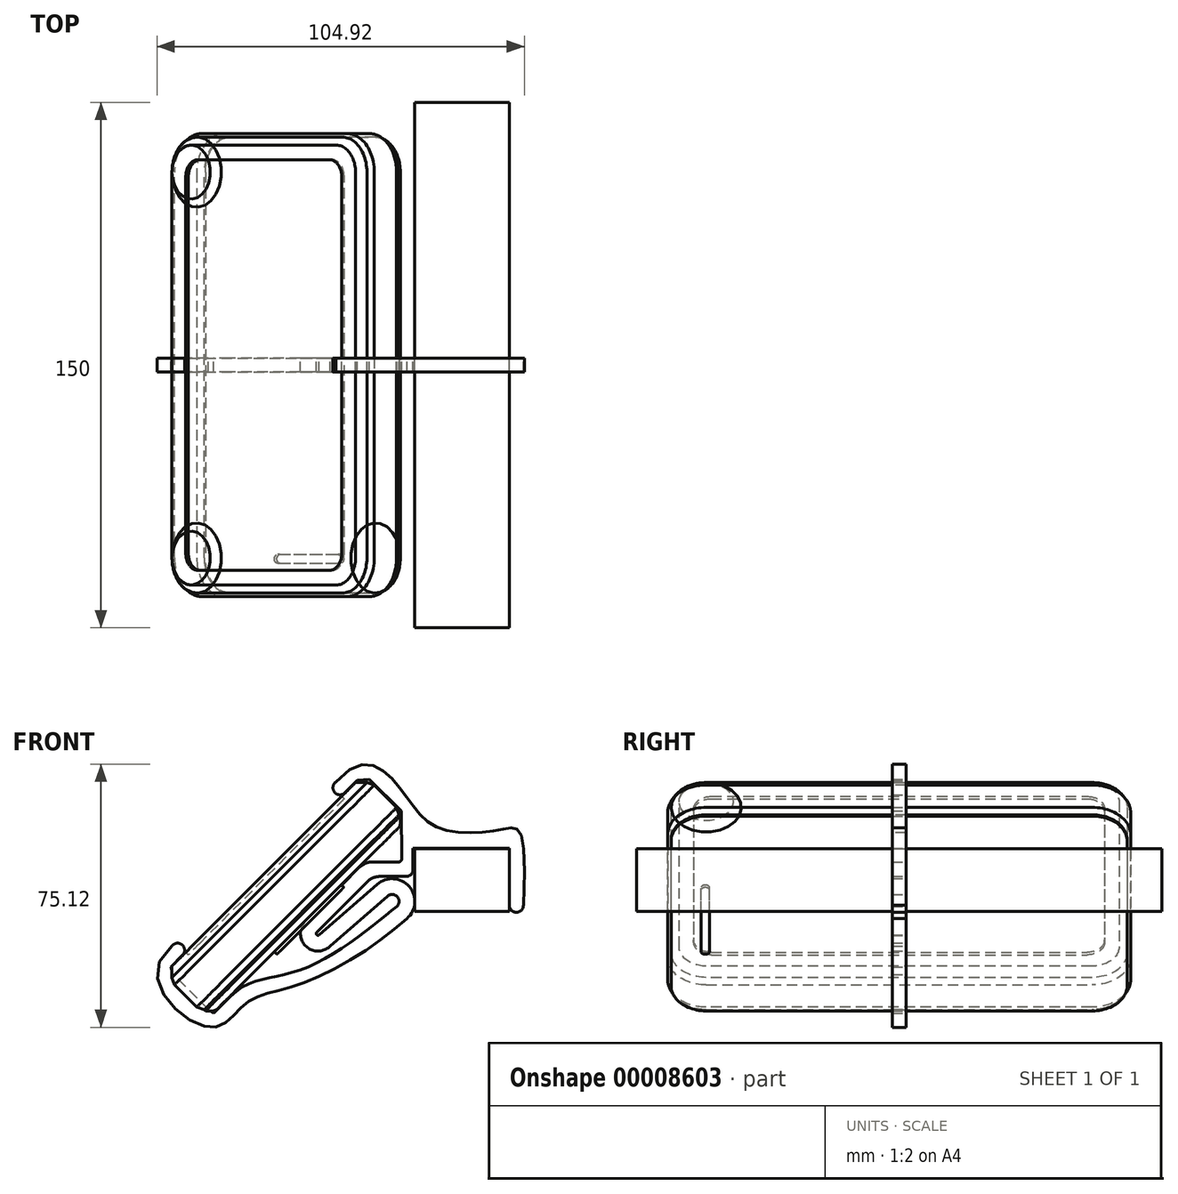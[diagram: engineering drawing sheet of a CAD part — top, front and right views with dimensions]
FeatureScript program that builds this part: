
annotation { "Feature Type Name" : "Feature", "Feature Type Description" : "" }
export const myFeature = defineFeature(function(context is Context, id is Id, definition is map)
    precondition{}
    {
        {
            var Q0;
            Q0=qCreatedBy(makeId("Right.planeOp"),FACE);
            var sketch = newSketch(context, id + "F0", { "sketchPlane" : qUnion([Q0])});
            skLineSegment(sketch, "E0", {"start": v(-84.74, 0) * mm, "end": v(84.74, 0) * mm, "construction": true});
            skSolve(sketch);
        }
        {
            var Q0;
            Q0=sQuery(id+"F0.wireOp",EDGE,"E0");
            cPlane(context, id + "F1", {"entities" : qUnion([Q0]), "cplaneType" : CPlaneType.LINE_ANGLE, "offset" : 150 * mm, "angle" : 315 * degree, "width" : 150 * mm, "height" : 150 * mm});
        }
        {
            var Q0;
            Q0=qCreatedBy(id+"F1.planeOp",FACE);
            var sketch = newSketch(context, id + "F2", { "sketchPlane" : qUnion([Q0])});
            skLineSegment(sketch, "E1.rect.bottom", {"start": v(55.1, -40.35) * mm, "end": v(-55.1, -40.35) * mm});
            skLineSegment(sketch, "E1.rect.top", {"start": v(55.1, 40.35) * mm, "end": v(-55.1, 40.35) * mm});
            skLineSegment(sketch, "E1.rect.left", {"start": v(66.1, -29.35) * mm, "end": v(66.1, 29.35) * mm});
            skLineSegment(sketch, "E1.rect.right", {"start": v(-66.1, -29.35) * mm, "end": v(-66.1, 29.35) * mm});
            skPoint(sketch, "E1.rect.middle", {"position": v(0, 0) * mm});
            skPoint(sketch, "E2.visualSharp", {"position": v(-66.1, 40.35) * mm});
            skArc(sketch, "E2.filletArc", {"start": v(-55.1, 40.35) * mm, "mid": v(-62.88, 37.13) * mm, "end": v(-66.1, 29.35) * mm});
            skPoint(sketch, "E3.visualSharp", {"position": v(66.1, 40.35) * mm});
            skArc(sketch, "E3.filletArc", {"start": v(66.1, 29.35) * mm, "mid": v(62.88, 37.13) * mm, "end": v(55.1, 40.35) * mm});
            skPoint(sketch, "E4.visualSharp", {"position": v(66.1, -40.35) * mm});
            skArc(sketch, "E4.filletArc", {"start": v(55.1, -40.35) * mm, "mid": v(62.88, -37.13) * mm, "end": v(66.1, -29.35) * mm});
            skPoint(sketch, "E5.visualSharp", {"position": v(-66.1, -40.35) * mm});
            skArc(sketch, "E5.filletArc", {"start": v(-66.1, -29.35) * mm, "mid": v(-62.88, -37.13) * mm, "end": v(-55.1, -40.35) * mm});
            skSolve(sketch);
        }
        {
            var Q0;
            Q0 = qSketchRegion(id + "F2", true);
            extrude(context, id + "F3", {"entities" : qUnion([Q0]), "oppositeDirection" : true, "depth" : 13 * mm});
        }
        {
            var Q0;
            Q0=makeQuery(id+"F3.opExtrude","CAP_EDGE",EDGE,{"disambiguationData":[OSD([sQuery(id+"F2.wireOp",EDGE,"E1.rect.right")])],"isStart":false});
            var Q1;
            Q1=makeQuery(id+"F3.opExtrude","CAP_EDGE",EDGE,{"disambiguationData":[OSD([sQuery(id+"F2.wireOp",EDGE,"E1.rect.right")])],"isStart":true});
            chamfer(context, id + "F4", {"entities" : qUnion([Q0, Q1]), "chamferType" : ChamferType.TWO_OFFSETS, "width1" : 1 * mm, "oppositeDirection" : false, "width2" : 2 * mm, "tangentPropagation" : true});
        }
        {
            var Q0;
            Q0=makeQuery(id+"F3.opExtrude","CAP_FACE",FACE,{"disambiguationData":[OSD([sQuery(id+"F2.wireOp",EDGE,"E1.rect.bottom"),sQuery(id+"F2.wireOp",EDGE,"E1.rect.top"),sQuery(id+"F2.wireOp",EDGE,"E1.rect.left"),sQuery(id+"F2.wireOp",EDGE,"E1.rect.right"),sQuery(id+"F2.wireOp",EDGE,"E2.filletArc"),sQuery(id+"F2.wireOp",EDGE,"E3.filletArc"),sQuery(id+"F2.wireOp",EDGE,"E4.filletArc"),sQuery(id+"F2.wireOp",EDGE,"E5.filletArc")])],"isStart":false});
            var sketch = newSketch(context, id + "F5", { "sketchPlane" : qUnion([Q0])});
            skLineSegment(sketch, "E6.0", {"start": v(55.1, 39.35) * mm, "end": v(-55.1, 39.35) * mm});
            skLineSegment(sketch, "E6.2", {"start": v(65.1, -29.35) * mm, "end": v(65.1, 29.35) * mm});
            skLineSegment(sketch, "E6.4", {"start": v(-55.1, -39.35) * mm, "end": v(55.1, -39.35) * mm});
            skLineSegment(sketch, "E6.6", {"start": v(-65.1, 29.35) * mm, "end": v(-65.1, -29.35) * mm});
            skArc(sketch, "E7.0", {"start": v(-55.1, 39.35) * mm, "mid": v(-62.17, 36.42) * mm, "end": v(-65.1, 29.35) * mm});
            skArc(sketch, "E7.1", {"start": v(65.1, 29.35) * mm, "mid": v(62.17, 36.42) * mm, "end": v(55.1, 39.35) * mm});
            skArc(sketch, "E7.2", {"start": v(55.1, -39.35) * mm, "mid": v(62.17, -36.42) * mm, "end": v(65.1, -29.35) * mm});
            skArc(sketch, "E7.3", {"start": v(-65.1, -29.35) * mm, "mid": v(-62.17, -36.42) * mm, "end": v(-55.1, -39.35) * mm});
            skSolve(sketch);
        }
        {
            var Q0;
            Q0 = qSketchRegion(id + "F5", true);
            extrude(context, id + "F6", {"entities" : qUnion([Q0]), "depth" : 2.5 * mm});
        }
        {
            var Q0;
            Q0=makeQuery(id+"F6.opExtrude","CAP_EDGE",EDGE,{"disambiguationData":[OSD([sQuery(id+"F5.wireOp",EDGE,"E6.2")])],"isStart":false});
            chamfer(context, id + "F7", {"entities" : qUnion([Q0]), "chamferType" : ChamferType.TWO_OFFSETS, "width1" : 2 * mm, "oppositeDirection" : false, "width2" : 2 * mm, "tangentPropagation" : true});
        }
        {
            var Q0;
            {var subQ0=sQuery(id+"F5.wireOp",EDGE,"E6.2");Q0=makeQuery(id+"F7.opChamfer","BLEND_EDGE",EDGE,{"blendedFrom":[makeQuery(id+"F6.opExtrude","CAP_EDGE",EDGE,{"disambiguationData":[OSD([subQ0])],"isStart":false}),makeQuery(id+"F6.opExtrude","CAP_FACE",FACE,{"disambiguationData":[OSD([sQuery(id+"F5.wireOp",EDGE,"E6.0"),sQuery(id+"F5.wireOp",EDGE,"E6.1"),subQ0,sQuery(id+"F5.wireOp",EDGE,"E6.3"),sQuery(id+"F5.wireOp",EDGE,"E6.4"),sQuery(id+"F5.wireOp",EDGE,"E6.5"),sQuery(id+"F5.wireOp",EDGE,"E6.6"),sQuery(id+"F5.wireOp",EDGE,"E6.7")])],"isStart":false})],"blendedInto":[makeQuery(id+"F6.opExtrude","CAP_FACE",FACE,{"disambiguationData":[OSD([sQuery(id+"F5.wireOp",EDGE,"E6.0"),sQuery(id+"F5.wireOp",EDGE,"E6.1"),subQ0,sQuery(id+"F5.wireOp",EDGE,"E6.3"),sQuery(id+"F5.wireOp",EDGE,"E6.4"),sQuery(id+"F5.wireOp",EDGE,"E6.5"),sQuery(id+"F5.wireOp",EDGE,"E6.6"),sQuery(id+"F5.wireOp",EDGE,"E6.7")])],"isStart":false})]});}
            fillet(context, id + "F8", {"entities" : qUnion([Q0]), "radius" : 2 * mm, "tangentPropagation" : true, "allowEdgeOverflow" : false});
        }
        {
            var Q0;
            Q0=makeQuery(id+"F3.opExtrude","CAP_FACE",FACE,{"disambiguationData":[OSD([sQuery(id+"F2.wireOp",EDGE,"E1.rect.bottom"),sQuery(id+"F2.wireOp",EDGE,"E1.rect.top"),sQuery(id+"F2.wireOp",EDGE,"E1.rect.left"),sQuery(id+"F2.wireOp",EDGE,"E1.rect.right"),sQuery(id+"F2.wireOp",EDGE,"E2.filletArc"),sQuery(id+"F2.wireOp",EDGE,"E3.filletArc"),sQuery(id+"F2.wireOp",EDGE,"E4.filletArc"),sQuery(id+"F2.wireOp",EDGE,"E5.filletArc")])],"isStart":true});
            var sketch = newSketch(context, id + "F9", { "sketchPlane" : qUnion([Q0])});
            skLineSegment(sketch, "E8.0", {"start": v(55.1, 39.35) * mm, "end": v(-55.1, 39.35) * mm});
            skLineSegment(sketch, "E8.2", {"start": v(65.1, -29.35) * mm, "end": v(65.1, 29.35) * mm});
            skLineSegment(sketch, "E8.4", {"start": v(-55.1, -39.35) * mm, "end": v(55.1, -39.35) * mm});
            skLineSegment(sketch, "E8.6", {"start": v(-65.1, 29.35) * mm, "end": v(-65.1, -29.35) * mm});
            skArc(sketch, "E9.0", {"start": v(-55.1, 39.35) * mm, "mid": v(-62.17, 36.42) * mm, "end": v(-65.1, 29.35) * mm});
            skArc(sketch, "E9.1", {"start": v(65.1, 29.35) * mm, "mid": v(62.17, 36.42) * mm, "end": v(55.1, 39.35) * mm});
            skArc(sketch, "E9.2", {"start": v(55.1, -39.35) * mm, "mid": v(62.17, -36.42) * mm, "end": v(65.1, -29.35) * mm});
            skArc(sketch, "E9.3", {"start": v(-65.1, -29.35) * mm, "mid": v(-62.17, -36.42) * mm, "end": v(-55.1, -39.35) * mm});
            skSolve(sketch);
        }
        {
            var Q0;
            Q0 = qSketchRegion(id + "F9", true);
            extrude(context, id + "F10", {"entities" : qUnion([Q0]), "depth" : 2.3 * mm});
        }
        {
            var Q0;
            Q0=makeQuery(id+"F10.opExtrude","CAP_EDGE",EDGE,{"disambiguationData":[OSD([sQuery(id+"F9.wireOp",EDGE,"E8.2")])],"isStart":false});
            chamfer(context, id + "F11", {"entities" : qUnion([Q0]), "chamferType" : ChamferType.TWO_OFFSETS, "width1" : 2.3 * mm, "oppositeDirection" : false, "width2" : 2.3 * mm, "tangentPropagation" : true});
        }
        {
            var Q0;
            Q0=makeQuery(id+"F6.opExtrude","CAP_FACE",FACE,{"disambiguationData":[OSD([sQuery(id+"F5.wireOp",EDGE,"E6.0"),sQuery(id+"F5.wireOp",EDGE,"E6.1"),sQuery(id+"F5.wireOp",EDGE,"E6.2"),sQuery(id+"F5.wireOp",EDGE,"E6.3"),sQuery(id+"F5.wireOp",EDGE,"E6.4"),sQuery(id+"F5.wireOp",EDGE,"E6.5"),sQuery(id+"F5.wireOp",EDGE,"E6.6"),sQuery(id+"F5.wireOp",EDGE,"E6.7")])],"isStart":false});
            var sketch = newSketch(context, id + "F12", { "sketchPlane" : qUnion([Q0])});
            skLineSegment(sketch, "E10.rect.left", {"start": v(-54.1, -12.25) * mm, "end": v(-54.1, 12.25) * mm});
            skLineSegment(sketch, "E10.rect.right", {"start": v(-56.6, -12.25) * mm, "end": v(-56.6, 12.25) * mm});
            skPoint(sketch, "E10.rect.middle", {"position": v(-55.35, 0) * mm});
            skArc(sketch, "E11", {"start": v(-54.1, 12.25) * mm, "mid": v(-55.35, 13.5) * mm, "end": v(-56.6, 12.25) * mm});
            skArc(sketch, "E12", {"start": v(-56.6, -12.25) * mm, "mid": v(-55.35, -13.5) * mm, "end": v(-54.1, -12.25) * mm});
            skSolve(sketch);
        }
        {
            var Q0;
            Q0 = qSketchRegion(id + "F12", true);
            extrude(context, id + "F13", {"entities" : qUnion([Q0]), "depth" : 1 * mm});
        }
        {
            var Q0;
            Q0=makeQuery(id+"F10.opExtrude","CAP_FACE",FACE,{"disambiguationData":[OSD([sQuery(id+"F9.wireOp",EDGE,"E8.0"),sQuery(id+"F9.wireOp",EDGE,"E8.1"),sQuery(id+"F9.wireOp",EDGE,"E8.2"),sQuery(id+"F9.wireOp",EDGE,"E8.3"),sQuery(id+"F9.wireOp",EDGE,"E8.4"),sQuery(id+"F9.wireOp",EDGE,"E8.5"),sQuery(id+"F9.wireOp",EDGE,"E8.6"),sQuery(id+"F9.wireOp",EDGE,"E8.7")])],"isStart":false});
            var sketch = newSketch(context, id + "F14", { "sketchPlane" : qUnion([Q0])});
            skLineSegment(sketch, "E13.rect.bottom", {"start": v(53.65, 31.5) * mm, "end": v(-53.65, 31.5) * mm});
            skLineSegment(sketch, "E13.rect.top", {"start": v(53.65, -31.5) * mm, "end": v(-53.65, -31.5) * mm});
            skLineSegment(sketch, "E13.rect.left", {"start": v(58.65, 26.5) * mm, "end": v(58.65, -26.5) * mm});
            skLineSegment(sketch, "E13.rect.right", {"start": v(-58.65, 26.5) * mm, "end": v(-58.65, -26.5) * mm});
            skPoint(sketch, "E13.rect.middle", {"position": v(0, 0) * mm});
            skPoint(sketch, "E14.visualSharp", {"position": v(-58.65, -31.5) * mm});
            skArc(sketch, "E14.filletArc", {"start": v(-58.65, -26.5) * mm, "mid": v(-57.19, -30.04) * mm, "end": v(-53.65, -31.5) * mm});
            skPoint(sketch, "E15.visualSharp", {"position": v(-58.65, 31.5) * mm});
            skArc(sketch, "E15.filletArc", {"start": v(-53.65, 31.5) * mm, "mid": v(-57.19, 30.04) * mm, "end": v(-58.65, 26.5) * mm});
            skPoint(sketch, "E16.visualSharp", {"position": v(58.65, 31.5) * mm});
            skArc(sketch, "E16.filletArc", {"start": v(58.65, 26.5) * mm, "mid": v(57.19, 30.04) * mm, "end": v(53.65, 31.5) * mm});
            skPoint(sketch, "E17.visualSharp", {"position": v(58.65, -31.5) * mm});
            skArc(sketch, "E17.filletArc", {"start": v(53.65, -31.5) * mm, "mid": v(57.19, -30.04) * mm, "end": v(58.65, -26.5) * mm});
            skSolve(sketch);
        }
        {
            var Q0;
            Q0 = qSketchRegion(id + "F14", true);
            extrude(context, id + "F15", {"entities" : qUnion([Q0]), "operationType" : NewBodyOperationType.REMOVE, "oppositeDirection" : true, "depth" : 1 * mm});
        }
        {
            var Q0;
            Q0=qCreatedBy(makeId("Front.planeOp"),FACE);
            var sketch = newSketch(context, id + "F16", { "sketchPlane" : qUnion([Q0])});
            skLineSegment(sketch, "E18.rect.bottom", {"start": v(68.5, -9) * mm, "end": v(41.5, -9) * mm});
            skLineSegment(sketch, "E18.rect.top", {"start": v(68.5, 9) * mm, "end": v(41.5, 9) * mm});
            skLineSegment(sketch, "E18.rect.left", {"start": v(68.5, -9) * mm, "end": v(68.5, 9) * mm});
            skLineSegment(sketch, "E18.rect.right", {"start": v(41.5, -9) * mm, "end": v(41.5, 9) * mm});
            skPoint(sketch, "E18.rect.middle", {"position": v(55, 0) * mm});
            skLineSegment(sketch, "E19", {"start": v(21.53, 24.92) * mm, "end": v(25.05, 28.44) * mm});
            skLineSegment(sketch, "E20", {"start": v(25.05, 28.44) * mm, "end": v(28.55, 28.8) * mm});
            skLineSegment(sketch, "E21", {"start": v(28.55, 28.8) * mm, "end": v(37.59, 19.76) * mm});
            skLineSegment(sketch, "E22", {"start": v(37.59, 19.76) * mm, "end": v(37.8, 6.16) * mm});
            skLineSegment(sketch, "E23", {"start": v(-17.45, -36.93) * mm, "end": v(-15.94, -38) * mm});
            skLineSegment(sketch, "E24", {"start": v(-17.45, -36.93) * mm, "end": v(-27.44, -26.94) * mm});
            skLineSegment(sketch, "E25", {"start": v(-27.44, -26.94) * mm, "end": v(-28.17, -24.78) * mm});
            skLineSegment(sketch, "E26", {"start": v(-28.17, -24.78) * mm, "end": v(-24.82, -21.43) * mm});
            skLineSegment(sketch, "E27.2", {"start": v(68.5, -7.24) * mm, "end": v(68.5, 9.01) * mm});
            skLineSegment(sketch, "E27.3", {"start": v(68.5, 9.01) * mm, "end": v(41, 9.01) * mm});
            skArc(sketch, "E28", {"start": v(18.97, 27.98) * mm, "mid": v(18.58, 25.05) * mm, "end": v(21.53, 24.92) * mm});
            skFitSpline(sketch, "E29", {"points": [v(18.97, 27.98) * mm, v(36.17, 27.6) * mm, v(47.66, 15.2) * mm, v(65.88, 14.4) * mm, v(72.51, -7.24) * mm], "startDerivative": vector(93.81, 110.27) * mm, "endDerivative": vector(-12.06, -266.09) * mm});
            skArc(sketch, "E30", {"start": v(68.51, -7.24) * mm, "mid": v(70.51, -9.24) * mm, "end": v(72.51, -7.24) * mm});
            skArc(sketch, "E31", {"start": v(-24.82, -21.43) * mm, "mid": v(-24.96, -18.47) * mm, "end": v(-27.89, -18.89) * mm});
            skFitSpline(sketch, "E32", {"points": [v(-27.89, -18.89) * mm, v(-18, -41.93) * mm, v(-6.76, -35.24) * mm, v(8.31, -29.91) * mm, v(39.27, -11) * mm], "startDerivative": vector(-124.18, -96.69) * mm, "endDerivative": vector(77.38, 70.92) * mm});
            skArc(sketch, "E33", {"start": v(10.31, -11.75) * mm, "mid": v(10.31, -18.82) * mm, "end": v(17.38, -18.82) * mm});
            skLineSegment(sketch, "E34", {"start": v(10.31, -11.75) * mm, "end": v(17.38, -18.82) * mm, "construction": true});
            skArc(sketch, "E35", {"start": v(13.5, -14.93) * mm, "mid": v(13.5, -15.64) * mm, "end": v(14.2, -15.64) * mm});
            skLineSegment(sketch, "E36", {"start": v(13.5, -14.93) * mm, "end": v(27.97, -0.45) * mm});
            skLineSegment(sketch, "E37", {"start": v(41.5, -9) * mm, "end": v(68.5, 9) * mm, "construction": true});
            skLineSegment(sketch, "E38", {"start": v(14.2, -15.64) * mm, "end": v(30.74, -1.22) * mm});
            skLineSegment(sketch, "E39", {"start": v(17.38, -18.82) * mm, "end": v(33.69, -4.6) * mm});
            skArc(sketch, "E40", {"start": v(36.31, -7.62) * mm, "mid": v(36.5, -4.8) * mm, "end": v(33.69, -4.6) * mm});
            skArc(sketch, "E41", {"start": v(39.27, -11) * mm, "mid": v(39.9, -1.85) * mm, "end": v(30.74, -1.22) * mm});
            skLineSegment(sketch, "E42", {"start": v(39.27, -11) * mm, "end": v(30.74, -1.22) * mm, "construction": true});
            skFitSpline(sketch, "E43", {"points": [v(36.31, -7.62) * mm, v(9.98, -25.26) * mm, v(-11.24, -33.3) * mm], "startDerivative": vector(-30.56, -24.35) * mm, "endDerivative": vector(-38.63, -38.63) * mm});
            skLineSegment(sketch, "E44.trimOffspring", {"start": v(-11.24, -33.3) * mm, "end": v(-15.94, -38) * mm});
            skLineSegment(sketch, "E45", {"start": v(68.51, -7.24) * mm, "end": v(72.51, -7.24) * mm, "construction": true});
            skLineSegment(sketch, "E46.top", {"start": v(31.5, 1) * mm, "end": v(39, 1.01) * mm});
            skLineSegment(sketch, "E46.right", {"start": v(41, 9.01) * mm, "end": v(41, 3.01) * mm});
            skArc(sketch, "E47.filletArc", {"start": v(31.5, 1) * mm, "mid": v(29.6, 0.63) * mm, "end": v(27.97, -0.45) * mm});
            skPoint(sketch, "E48.visualSharp", {"position": v(41, 1.01) * mm});
            skArc(sketch, "E48.filletArc", {"start": v(39, 1.01) * mm, "mid": v(40.41, 1.6) * mm, "end": v(41, 3.01) * mm});
            skLineSegment(sketch, "E49.top", {"start": v(29.27, 5.14) * mm, "end": v(36.8, 5.14) * mm});
            skLineSegment(sketch, "E50.trimOffspring", {"start": v(25.74, 3.68) * mm, "end": v(10.31, -11.75) * mm});
            skArc(sketch, "E51.filletArc", {"start": v(36.8, 5.14) * mm, "mid": v(37.5, 5.44) * mm, "end": v(37.8, 6.16) * mm});
            skArc(sketch, "E52.filletArc", {"start": v(29.27, 5.14) * mm, "mid": v(27.36, 4.76) * mm, "end": v(25.74, 3.68) * mm});
            skSolve(sketch);
        }
        {
            var Q0;
            Q0=makeQuery(id+"F16.imprint","IMPRINT",FACE,{"disambiguationData":[TD([[makeQuery(id+"F16.imprint","IMPRINT",EDGE,{"derivedFrom":sQuery(id+"F16.wireOp",EDGE,"E19")}),1.0]])]});
            extrude(context, id + "F17", {"entities" : qUnion([Q0]), "endBound" : BoundingType.SYMMETRIC, "depth" : 4 * mm});
        }
        {
            var Q0;
            Q0=makeQuery(id+"F16.imprint","IMPRINT",FACE,{"disambiguationData":[TD([[makeQuery(id+"F16.imprint","IMPRINT",EDGE,{"derivedFrom":sQuery(id+"F16.wireOp",EDGE,"E18.rect.bottom")}),-1.0]])]});
            extrude(context, id + "F18", {"entities" : qUnion([Q0]), "endBound" : BoundingType.SYMMETRIC, "depth" : 150 * mm});
        }
    });
